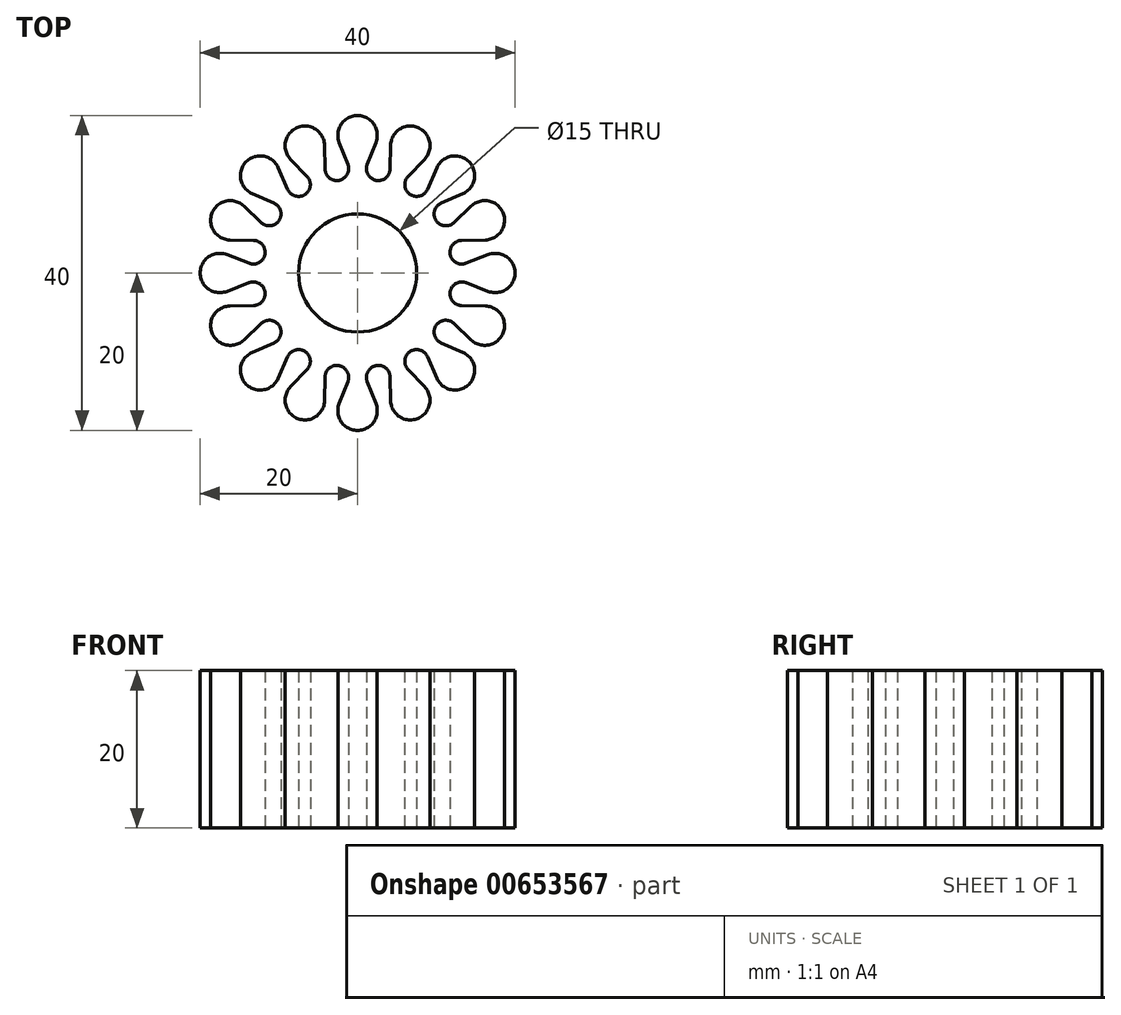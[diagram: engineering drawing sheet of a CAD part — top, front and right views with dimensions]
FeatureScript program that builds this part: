
annotation { "Feature Type Name" : "Feature", "Feature Type Description" : "" }
export const myFeature = defineFeature(function(context is Context, id is Id, definition is map)
    precondition{}
    {
        {
            var Q0;
            Q0=qCreatedBy(makeId("Top.planeOp"),FACE);
            var sketch = newSketch(context, id + "F0", { "sketchPlane" : qUnion([Q0])});
            skCircle(sketch, "E0", {"center": v(0, 0) * mm, "radius": 20 * mm, "construction": true});
            skCircle(sketch, "E1", {"center": v(0, 0) * mm, "radius": 12 * mm, "construction": true});
            skCircle(sketch, "E2", {"center": v(0, 0) * mm, "radius": 15 * mm, "construction": true});
            skArc(sketch, "E3", {"start": v(-16.6, 2.33) * mm, "mid": v(-20, 0) * mm, "end": v(-16.6, -2.33) * mm});
            skLineSegment(sketch, "E4", {"start": v(0, 0) * mm, "end": v(-17.5, 0) * mm, "construction": true});
            skLineSegment(sketch, "E5", {"start": v(0, 0) * mm, "end": v(-13.24, 2.63) * mm, "construction": true});
            skArc(sketch, "E6", {"start": v(-13.78, 1.24) * mm, "mid": v(-11.77, 2.34) * mm, "end": v(-13.2, 4.13) * mm});
            skLineSegment(sketch, "E7", {"start": v(-16.6, 2.33) * mm, "end": v(-13.78, 1.24) * mm});
            skLineSegment(sketch, "E8", {"start": v(-13.24, -2.63) * mm, "end": v(0, 0) * mm, "construction": true});
            skLineSegment(sketch, "E9", {"start": v(-16.6, -2.33) * mm, "end": v(-13.78, -1.24) * mm});
            skLineSegment(sketch, "E10.1.0", {"start": v(-16.22, -4.2) * mm, "end": v(-13.2, -4.13) * mm});
            skArc(sketch, "E10.1.1", {"start": v(-16.22, -4.2) * mm, "mid": v(-18.48, -7.65) * mm, "end": v(-14.44, -8.5) * mm});
            skLineSegment(sketch, "E10.1.2", {"start": v(-14.44, -8.5) * mm, "end": v(-12.26, -6.42) * mm});
            skLineSegment(sketch, "E10.2.0", {"start": v(-13.38, -10.09) * mm, "end": v(-10.62, -8.87) * mm});
            skArc(sketch, "E10.2.1", {"start": v(-13.38, -10.09) * mm, "mid": v(-14.14, -14.14) * mm, "end": v(-10.09, -13.38) * mm});
            skLineSegment(sketch, "E10.2.2", {"start": v(-10.09, -13.38) * mm, "end": v(-8.87, -10.62) * mm});
            skLineSegment(sketch, "E10.3.0", {"start": v(-8.5, -14.44) * mm, "end": v(-6.42, -12.26) * mm});
            skArc(sketch, "E10.3.1", {"start": v(-8.5, -14.44) * mm, "mid": v(-7.65, -18.48) * mm, "end": v(-4.2, -16.22) * mm});
            skLineSegment(sketch, "E10.3.2", {"start": v(-4.2, -16.22) * mm, "end": v(-4.13, -13.2) * mm});
            skLineSegment(sketch, "E10.4.0", {"start": v(-2.33, -16.6) * mm, "end": v(-1.24, -13.78) * mm});
            skArc(sketch, "E10.4.1", {"start": v(-2.33, -16.6) * mm, "mid": v(0, -20) * mm, "end": v(2.33, -16.6) * mm});
            skLineSegment(sketch, "E10.4.2", {"start": v(2.33, -16.6) * mm, "end": v(1.24, -13.78) * mm});
            skLineSegment(sketch, "E10.5.0", {"start": v(4.2, -16.22) * mm, "end": v(4.13, -13.2) * mm});
            skArc(sketch, "E10.5.1", {"start": v(4.2, -16.22) * mm, "mid": v(7.65, -18.48) * mm, "end": v(8.5, -14.44) * mm});
            skLineSegment(sketch, "E10.5.2", {"start": v(8.5, -14.44) * mm, "end": v(6.42, -12.26) * mm});
            skLineSegment(sketch, "E10.6.0", {"start": v(10.09, -13.38) * mm, "end": v(8.87, -10.62) * mm});
            skArc(sketch, "E10.6.1", {"start": v(10.09, -13.38) * mm, "mid": v(14.14, -14.14) * mm, "end": v(13.38, -10.09) * mm});
            skLineSegment(sketch, "E10.6.2", {"start": v(13.38, -10.09) * mm, "end": v(10.62, -8.87) * mm});
            skLineSegment(sketch, "E10.7.0", {"start": v(14.44, -8.5) * mm, "end": v(12.26, -6.42) * mm});
            skArc(sketch, "E10.7.1", {"start": v(14.44, -8.5) * mm, "mid": v(18.48, -7.65) * mm, "end": v(16.22, -4.2) * mm});
            skLineSegment(sketch, "E10.7.2", {"start": v(16.22, -4.2) * mm, "end": v(13.2, -4.13) * mm});
            skLineSegment(sketch, "E10.8.0", {"start": v(16.6, -2.33) * mm, "end": v(13.78, -1.24) * mm});
            skArc(sketch, "E10.8.1", {"start": v(16.6, -2.33) * mm, "mid": v(20, 0) * mm, "end": v(16.6, 2.33) * mm});
            skLineSegment(sketch, "E10.8.2", {"start": v(16.6, 2.33) * mm, "end": v(13.78, 1.24) * mm});
            skLineSegment(sketch, "E10.9.0", {"start": v(16.22, 4.2) * mm, "end": v(13.2, 4.13) * mm});
            skArc(sketch, "E10.9.1", {"start": v(16.22, 4.2) * mm, "mid": v(18.48, 7.65) * mm, "end": v(14.44, 8.5) * mm});
            skLineSegment(sketch, "E10.9.2", {"start": v(14.44, 8.5) * mm, "end": v(12.26, 6.42) * mm});
            skLineSegment(sketch, "E10.10.0", {"start": v(13.38, 10.09) * mm, "end": v(10.62, 8.87) * mm});
            skArc(sketch, "E10.10.1", {"start": v(13.38, 10.09) * mm, "mid": v(14.14, 14.14) * mm, "end": v(10.09, 13.38) * mm});
            skLineSegment(sketch, "E10.10.2", {"start": v(10.09, 13.38) * mm, "end": v(8.87, 10.62) * mm});
            skLineSegment(sketch, "E10.11.0", {"start": v(8.5, 14.44) * mm, "end": v(6.42, 12.26) * mm});
            skArc(sketch, "E10.11.1", {"start": v(8.5, 14.44) * mm, "mid": v(7.65, 18.48) * mm, "end": v(4.2, 16.22) * mm});
            skLineSegment(sketch, "E10.11.2", {"start": v(4.2, 16.22) * mm, "end": v(4.13, 13.2) * mm});
            skLineSegment(sketch, "E10.12.0", {"start": v(2.33, 16.6) * mm, "end": v(1.24, 13.78) * mm});
            skArc(sketch, "E10.12.1", {"start": v(2.33, 16.6) * mm, "mid": v(0, 20) * mm, "end": v(-2.33, 16.6) * mm});
            skLineSegment(sketch, "E10.12.2", {"start": v(-2.33, 16.6) * mm, "end": v(-1.24, 13.78) * mm});
            skLineSegment(sketch, "E10.13.0", {"start": v(-4.2, 16.22) * mm, "end": v(-4.13, 13.2) * mm});
            skArc(sketch, "E10.13.1", {"start": v(-4.2, 16.22) * mm, "mid": v(-7.65, 18.48) * mm, "end": v(-8.5, 14.44) * mm});
            skLineSegment(sketch, "E10.13.2", {"start": v(-8.5, 14.44) * mm, "end": v(-6.42, 12.26) * mm});
            skLineSegment(sketch, "E10.14.0", {"start": v(-10.09, 13.38) * mm, "end": v(-8.87, 10.62) * mm});
            skArc(sketch, "E10.14.1", {"start": v(-10.09, 13.38) * mm, "mid": v(-14.14, 14.14) * mm, "end": v(-13.38, 10.09) * mm});
            skLineSegment(sketch, "E10.14.2", {"start": v(-13.38, 10.09) * mm, "end": v(-10.62, 8.87) * mm});
            skLineSegment(sketch, "E10.15.0", {"start": v(-14.44, 8.5) * mm, "end": v(-12.26, 6.42) * mm});
            skArc(sketch, "E10.15.1", {"start": v(-14.44, 8.5) * mm, "mid": v(-18.48, 7.65) * mm, "end": v(-16.22, 4.2) * mm});
            skLineSegment(sketch, "E10.15.2", {"start": v(-16.22, 4.2) * mm, "end": v(-13.2, 4.13) * mm});
            skArc(sketch, "E11.1.0", {"start": v(-13.2, -4.13) * mm, "mid": v(-11.77, -2.34) * mm, "end": v(-13.78, -1.24) * mm});
            skArc(sketch, "E11.2.0", {"start": v(-10.62, -8.87) * mm, "mid": v(-9.98, -6.67) * mm, "end": v(-12.26, -6.42) * mm});
            skArc(sketch, "E11.3.0", {"start": v(-6.42, -12.26) * mm, "mid": v(-6.67, -9.98) * mm, "end": v(-8.87, -10.62) * mm});
            skArc(sketch, "E11.4.0", {"start": v(-1.24, -13.78) * mm, "mid": v(-2.34, -11.77) * mm, "end": v(-4.13, -13.2) * mm});
            skArc(sketch, "E11.5.0", {"start": v(4.13, -13.2) * mm, "mid": v(2.34, -11.77) * mm, "end": v(1.24, -13.78) * mm});
            skArc(sketch, "E11.6.0", {"start": v(8.87, -10.62) * mm, "mid": v(6.67, -9.98) * mm, "end": v(6.42, -12.26) * mm});
            skArc(sketch, "E11.7.0", {"start": v(12.26, -6.42) * mm, "mid": v(9.98, -6.67) * mm, "end": v(10.62, -8.87) * mm});
            skArc(sketch, "E11.8.0", {"start": v(13.78, -1.24) * mm, "mid": v(11.77, -2.34) * mm, "end": v(13.2, -4.13) * mm});
            skArc(sketch, "E11.9.0", {"start": v(13.2, 4.13) * mm, "mid": v(11.77, 2.34) * mm, "end": v(13.78, 1.24) * mm});
            skArc(sketch, "E11.10.0", {"start": v(10.62, 8.87) * mm, "mid": v(9.98, 6.67) * mm, "end": v(12.26, 6.42) * mm});
            skArc(sketch, "E11.11.0", {"start": v(6.42, 12.26) * mm, "mid": v(6.67, 9.98) * mm, "end": v(8.87, 10.62) * mm});
            skArc(sketch, "E11.12.0", {"start": v(1.24, 13.78) * mm, "mid": v(2.34, 11.77) * mm, "end": v(4.13, 13.2) * mm});
            skArc(sketch, "E11.13.0", {"start": v(-4.13, 13.2) * mm, "mid": v(-2.34, 11.77) * mm, "end": v(-1.24, 13.78) * mm});
            skArc(sketch, "E11.14.0", {"start": v(-8.87, 10.62) * mm, "mid": v(-6.67, 9.98) * mm, "end": v(-6.42, 12.26) * mm});
            skArc(sketch, "E11.15.0", {"start": v(-12.26, 6.42) * mm, "mid": v(-9.98, 6.67) * mm, "end": v(-10.62, 8.87) * mm});
            skCircle(sketch, "E12", {"center": v(0, 0) * mm, "radius": 7.5 * mm});
            skSolve(sketch);
        }
        {
            var Q0;
            Q0 = qSketchRegion(id + "F0", true);
            extrude(context, id + "F1", {"entities" : qUnion([Q0]), "depth" : 20 * mm, "offsetDistance" : 25 * mm});
        }
    });
